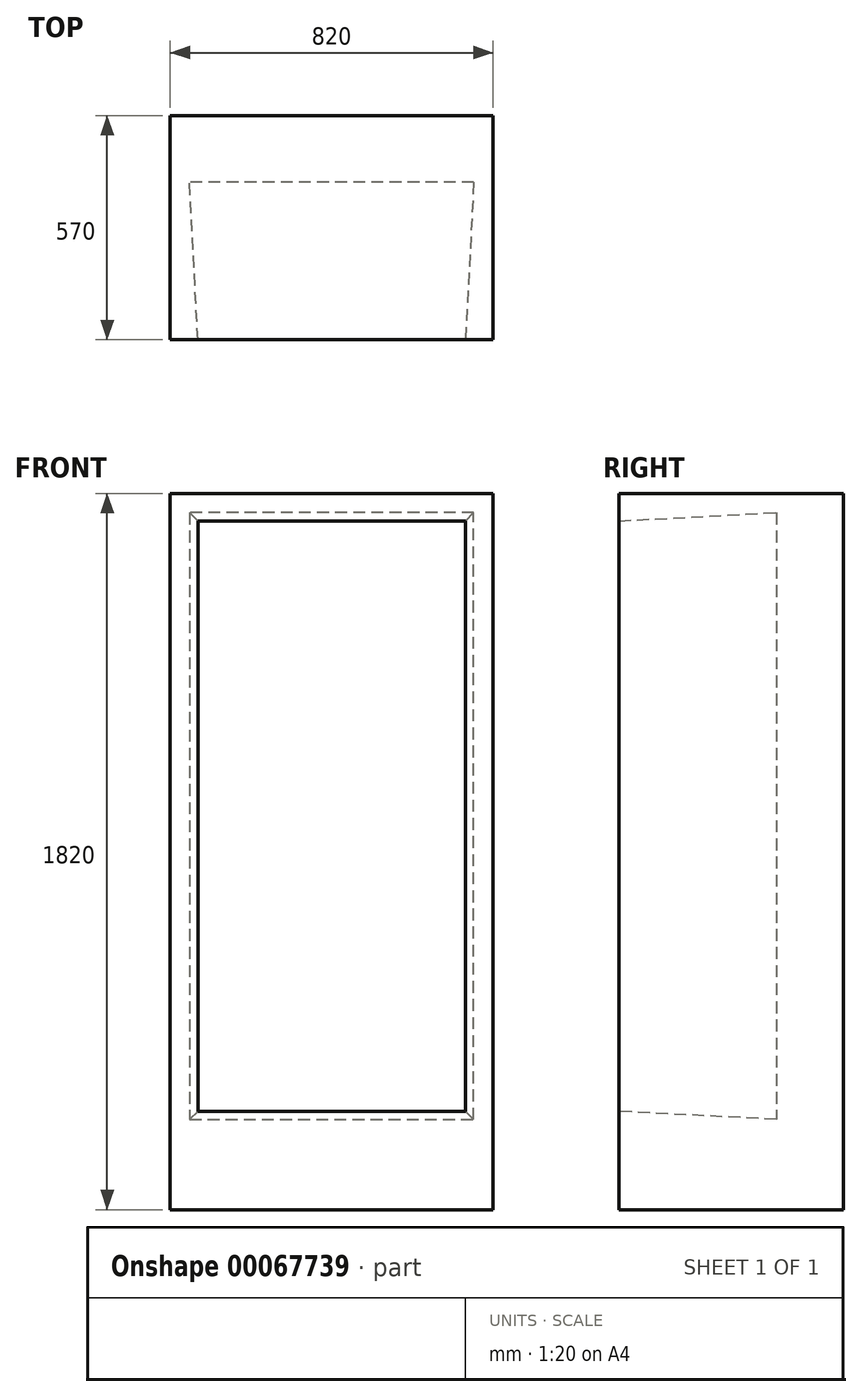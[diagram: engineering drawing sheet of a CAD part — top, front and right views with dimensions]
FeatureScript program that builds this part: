
annotation { "Feature Type Name" : "Feature", "Feature Type Description" : "" }
export const myFeature = defineFeature(function(context is Context, id is Id, definition is map)
    precondition{}
    {
        {
            var Q0;
            Q0=qCreatedBy(makeId("Front.planeOp"),FACE);
            var sketch = newSketch(context, id + "F0", { "sketchPlane" : qUnion([Q0])});
            skLineSegment(sketch, "E0", {"start": v(0, 0) * mm, "end": v(820, 0) * mm});
            skLineSegment(sketch, "E1", {"start": v(820, 0) * mm, "end": v(820, 1820) * mm});
            skLineSegment(sketch, "E2", {"start": v(820, 1820) * mm, "end": v(0, 1820) * mm});
            skLineSegment(sketch, "E3", {"start": v(0, 1820) * mm, "end": v(0, 0) * mm});
            skSolve(sketch);
        }
        {
            var Q0;
            Q0=makeQuery(id+"F0.imprint","IMPRINT",FACE,{"disambiguationData":[TD([[makeQuery(id+"F0.imprint","IMPRINT",EDGE,{"derivedFrom":sQuery(id+"F0.wireOp",EDGE,"E0")}),1.0]])]});
            extrude(context, id + "F1", {"entities" : qUnion([Q0]), "depth" : 570 * mm});
        }
        {
            var Q0;
            Q0=makeQuery(id+"F1.opExtrude","CAP_FACE",FACE,{"disambiguationData":[OSD([sQuery(id+"F0.wireOp",EDGE,"E0"),sQuery(id+"F0.wireOp",EDGE,"E1"),sQuery(id+"F0.wireOp",EDGE,"E2"),sQuery(id+"F0.wireOp",EDGE,"E3")])],"isStart":false});
            var sketch = newSketch(context, id + "F2", { "sketchPlane" : qUnion([Q0])});
            skLineSegment(sketch, "E4.bottom", {"start": v(70, 1750) * mm, "end": v(750, 1750) * mm});
            skLineSegment(sketch, "E4.top", {"start": v(70, 250) * mm, "end": v(750, 250) * mm});
            skLineSegment(sketch, "E4.left", {"start": v(70, 1750) * mm, "end": v(70, 250) * mm});
            skLineSegment(sketch, "E4.right", {"start": v(750, 1750) * mm, "end": v(750, 250) * mm});
            skSolve(sketch);
        }
        {
            var Q0;
            Q0=makeQuery(id+"F2.imprint","IMPRINT",FACE,{"disambiguationData":[TD([[makeQuery(id+"F2.imprint","IMPRINT",EDGE,{"derivedFrom":sQuery(id+"F2.wireOp",EDGE,"E4.bottom")}),-1.0]])]});
            extrude(context, id + "F3", {"entities" : qUnion([Q0]), "operationType" : NewBodyOperationType.REMOVE, "oppositeDirection" : true, "depth" : 400 * mm, "hasDraft" : true, "draftAngle" : 3 * degree});
        }
    });
